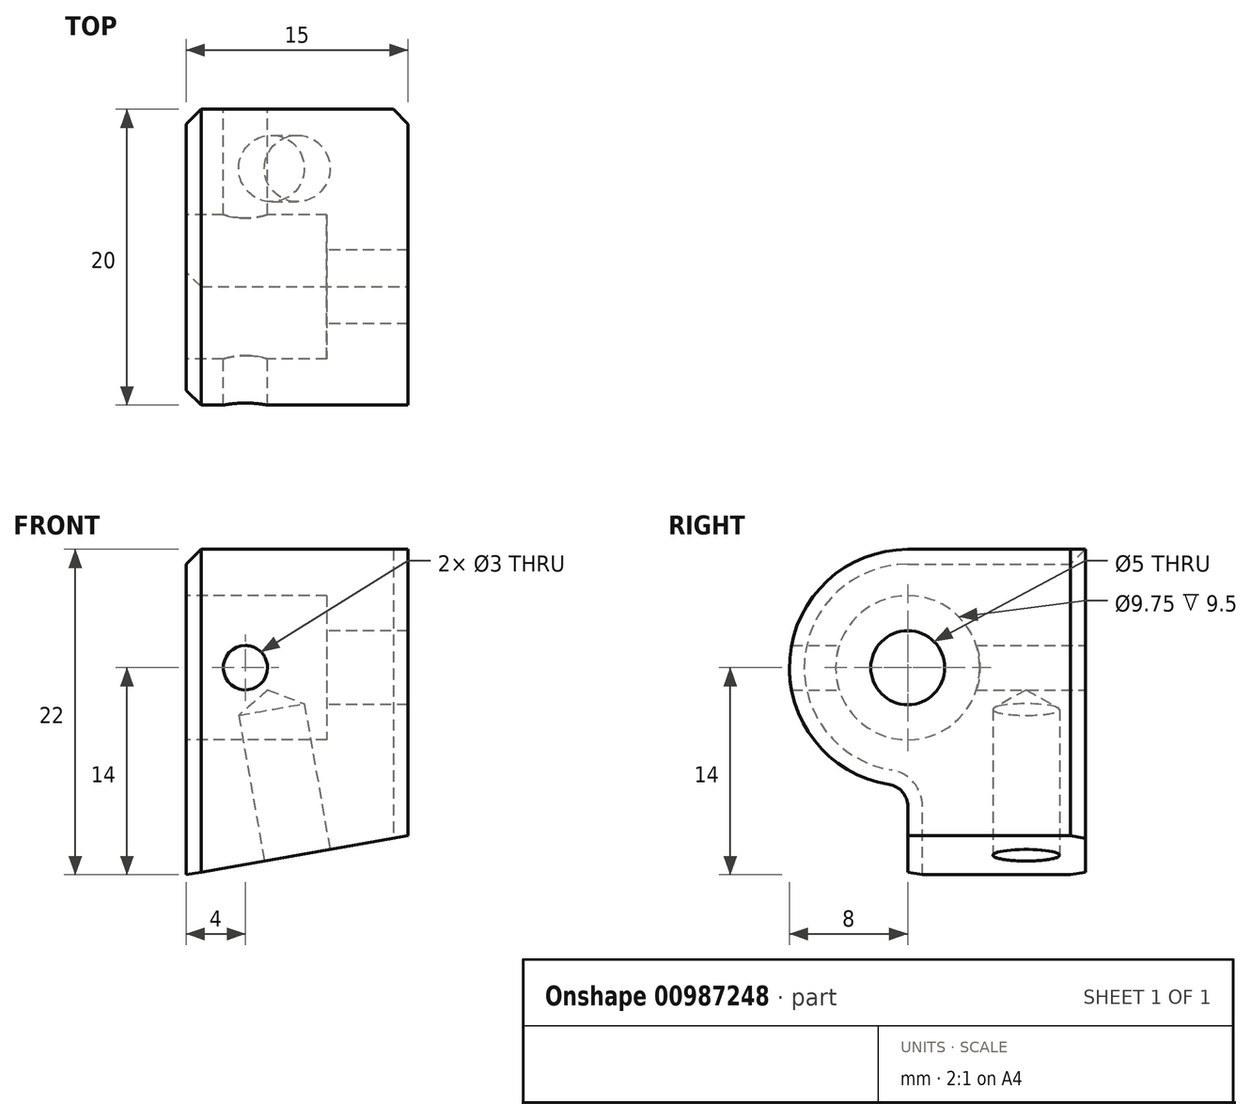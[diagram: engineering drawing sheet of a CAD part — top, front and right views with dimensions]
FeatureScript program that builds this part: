
annotation { "Feature Type Name" : "Feature", "Feature Type Description" : "" }
export const myFeature = defineFeature(function(context is Context, id is Id, definition is map)
    precondition{}
    {
        {
            var Q0;
            Q0=qCreatedBy(makeId("Front.planeOp"),FACE);
            var sketch = newSketch(context, id + "F0", { "sketchPlane" : qUnion([Q0])});
            skLineSegment(sketch, "E0", {"start": v(-7.5, 0) * mm, "end": v(-7.5, -22) * mm});
            skLineSegment(sketch, "E1", {"start": v(-7.5, -22) * mm, "end": v(7.5, -19.36) * mm});
            skLineSegment(sketch, "E2", {"start": v(7.5, -19.36) * mm, "end": v(7.5, 0) * mm});
            skLineSegment(sketch, "E3", {"start": v(7.5, 0) * mm, "end": v(-7.5, 0) * mm});
            skSolve(sketch);
        }
        {
            var Q0;
            Q0=makeQuery(id+"F0.imprint","IMPRINT",FACE,{"disambiguationData":[TD([[makeQuery(id+"F0.imprint","IMPRINT",EDGE,{"derivedFrom":sQuery(id+"F0.wireOp",EDGE,"E0")}),1.0]])]});
            extrude(context, id + "F1", {"entities" : qUnion([Q0]), "oppositeDirection" : true, "depth" : 20 * mm, "offsetDistance" : 25 * mm});
        }
        {
            var Q0;
            Q0=makeQuery(id+"F1.opExtrude","SWEPT_FACE",FACE,{"disambiguationData":[OSD([sQuery(id+"F0.wireOp",EDGE,"E0")])]});
            var sketch = newSketch(context, id + "F2", { "sketchPlane" : qUnion([Q0])});
            skPoint(sketch, "E4", {"position": v(-8, -8) * mm});
            skSolve(sketch);
        }
        {
            var Q0;
            Q0=sQuery(id+"F2.wireOp",VERTEX,"E4");
            var Q1;
            Q1=makeQuery(id+"F1.opExtrude","SWEPT_BODY",BODY,{"disambiguationData":[OSD([sQuery(id+"F0.wireOp",EDGE,"E0"),sQuery(id+"F0.wireOp",EDGE,"E1"),sQuery(id+"F0.wireOp",EDGE,"E2"),sQuery(id+"F0.wireOp",EDGE,"E3")])]});
            hole(context, id + "F3", {"style" : HoleStyle.C_BORE, "endStyle" : HoleEndStyle.THROUGH, "holeDiameter" : 5 * mm, "cBoreDiameter" : 9.75 * mm, "cBoreDepth" : 9.5 * mm, "majorDiameter" : 5 * mm, "isTappedThrough" : true, "tappedDepth" : 22.6 * mm, "tapClearance" : 3, "locations" : qUnion([Q0]), "scope" : qUnion([Q1])});
        }
        {
            var Q0;
            Q0=makeQuery(id+"F1.opExtrude","SWEPT_FACE",FACE,{"disambiguationData":[OSD([sQuery(id+"F0.wireOp",EDGE,"E1")])]});
            var sketch = newSketch(context, id + "F4", { "sketchPlane" : qUnion([Q0])});
            skPoint(sketch, "E5", {"position": v(-3.6, -16) * mm});
            skSolve(sketch);
        }
        {
            var Q0;
            Q0=sQuery(id+"F4.wireOp",VERTEX,"E5");
            var Q1;
            Q1=makeQuery(id+"F1.opExtrude","SWEPT_BODY",BODY,{"disambiguationData":[OSD([sQuery(id+"F0.wireOp",EDGE,"E0"),sQuery(id+"F0.wireOp",EDGE,"E1"),sQuery(id+"F0.wireOp",EDGE,"E2"),sQuery(id+"F0.wireOp",EDGE,"E3")])]});
            hole(context, id + "F5", {"style" : HoleStyle.SIMPLE, "endStyle" : HoleEndStyle.BLIND, "standardTappedOrClearance" : lookupTablePath({ "standard" : "ISO", "engagement" : "50%", "pitch" : "0.8 mm", "size" : "M5", "type" : "Tapped" }), "standardBlindInLast" : lookupTablePath({ "standard" : "ISO", "fit" : "Normal", "engagement" : "50%", "pitch" : "0.8 mm", "size" : "M5", "type" : "Clearance & tapped" }), "holeDiameter" : 4.5 * mm, "majorDiameter" : 5 * mm, "showTappedDepth" : true, "holeDepth" : 10 * mm, "isTappedThrough" : true, "tappedDepth" : 8.4 * mm, "tapClearance" : 2, "locations" : qUnion([Q0]), "scope" : qUnion([Q1])});
        }
        {
            var Q0;
            Q0=makeQuery(id+"F1.opExtrude","CAP_FACE",FACE,{"disambiguationData":[OSD([sQuery(id+"F0.wireOp",EDGE,"E0"),sQuery(id+"F0.wireOp",EDGE,"E1"),sQuery(id+"F0.wireOp",EDGE,"E2"),sQuery(id+"F0.wireOp",EDGE,"E3")])],"isStart":false});
            var sketch = newSketch(context, id + "F6", { "sketchPlane" : qUnion([Q0])});
            skCircle(sketch, "E6", {"center": v(3.5, -8) * mm, "radius": 1.5 * mm});
            skSolve(sketch);
        }
        {
            var Q0;
            Q0=makeQuery(id+"F6.imprint","IMPRINT",FACE,{"disambiguationData":[TD([[makeQuery(id+"F6.imprint","IMPRINT",EDGE,{"derivedFrom":sQuery(id+"F6.wireOp",EDGE,"E6")}),1.0]])]});
            extrude(context, id + "F7", {"entities" : qUnion([Q0]), "operationType" : NewBodyOperationType.REMOVE, "oppositeDirection" : true, "depth" : 25 * mm, "offsetDistance" : 25 * mm});
        }
        {
            var Q0;
            Q0=makeQuery(id+"F1.opExtrude","SWEPT_FACE",FACE,{"disambiguationData":[OSD([sQuery(id+"F0.wireOp",EDGE,"E0")])]});
            var sketch = newSketch(context, id + "F8", { "sketchPlane" : qUnion([Q0])});
            skLineSegment(sketch, "E7.bottom", {"start": v(-8, -16) * mm, "end": v(-8, -16) * mm});
            skLineSegment(sketch, "E8", {"start": v(-20, 0) * mm, "end": v(-20, -22) * mm});
            skLineSegment(sketch, "E9", {"start": v(-20, -22) * mm, "end": v(-8, -22) * mm});
            skLineSegment(sketch, "E10", {"start": v(-20, 0) * mm, "end": v(-8, 0) * mm});
            skArc(sketch, "E11", {"start": v(-6.74, -15.9) * mm, "mid": v(-0.03, -7.37) * mm, "end": v(-8, 0) * mm});
            skLineSegment(sketch, "E12", {"start": v(-8, -17.38) * mm, "end": v(-8, -22) * mm});
            skArc(sketch, "E13", {"start": v(-6.74, -15.9) * mm, "mid": v(-7.64, -16.4) * mm, "end": v(-8, -17.38) * mm});
            skSolve(sketch);
        }
        {
            var Q0;
            {var subQ0=sQuery(id+"F8.wireOp",EDGE,"E11");var subQ1=sQuery(id+"F0.wireOp",EDGE,"E0");var subQ4=makeQuery(id+"F1.opExtrude","CAP_EDGE",EDGE,{"disambiguationData":[OSD([subQ1])],"isStart":true});var subQ5=makeQuery(id+"F8.imprint","INTERSECT",VERTEX,{"derivedFrom":[subQ4,subQ0]});Q0=makeQuery(id+"F8.imprint","IMPRINT",FACE,{"disambiguationData":[TD([[makeQuery(id+"F8.imprint","IMPRINT",EDGE,{"disambiguationData":[TD([[subQ5,1.0]])],"derivedFrom":subQ4}),-1.0]])]});}
            var Q1;
            {var subQ0=sQuery(id+"F8.wireOp",EDGE,"E12");Q1=makeQuery(id+"F8.imprint","IMPRINT",FACE,{"disambiguationData":[TD([[makeQuery(id+"F8.imprint","IMPRINT",EDGE,{"derivedFrom":subQ0}),1.0]])]});}
            extrude(context, id + "F9", {"entities" : qUnion([Q0, Q1]), "operationType" : NewBodyOperationType.REMOVE, "endBound" : BoundingType.THROUGH_ALL, "oppositeDirection" : true, "depth" : 25 * mm, "offsetDistance" : 25 * mm});
        }
        {
            var Q0;
            Q0=makeQuery(id+"F3.hole-0.boolean.opBoolean","COPY",EDGE,{"derivedFrom":makeQuery(id+"F3.hole-0.opRevolve","SWEPT_EDGE",EDGE,{"disambiguationData":[OSD([sQuery(id+"F3.hole-0.sketch.wireOp",EDGE,"cbore_start_line_2"),sQuery(id+"F3.hole-0.sketch.wireOp",EDGE,"cbore_start_line_3")])]})});
            var Q1;
            Q1=makeQuery(id+"F1.opExtrude","CAP_EDGE",EDGE,{"disambiguationData":[OSD([sQuery(id+"F0.wireOp",EDGE,"E2")])],"isStart":false});
            var Q2;
            Q2=makeQuery(id+"F1.opExtrude","CAP_EDGE",EDGE,{"disambiguationData":[OSD([sQuery(id+"F0.wireOp",EDGE,"E0")])],"isStart":false});
            var Q3;
            Q3=makeQuery(id+"F1.opExtrude","SWEPT_EDGE",EDGE,{"disambiguationData":[OSD([sQuery(id+"F0.wireOp",EDGE,"E0"),sQuery(id+"F0.wireOp",EDGE,"E3")])]});
            var Q4;
            Q4=makeQuery(id+"F9.boolean.opBoolean","COPY",EDGE,{"derivedFrom":makeQuery(id+"F9.opExtrude","CAP_EDGE",EDGE,{"disambiguationData":[OSD([sQuery(id+"F8.wireOp",EDGE,"E12")])],"isStart":true})});
            chamfer(context, id + "F10", {"entities" : qUnion([Q0, Q1, Q2, Q3, Q4]), "width" : 1 * mm, "tangentPropagation" : true});
        }
    });
